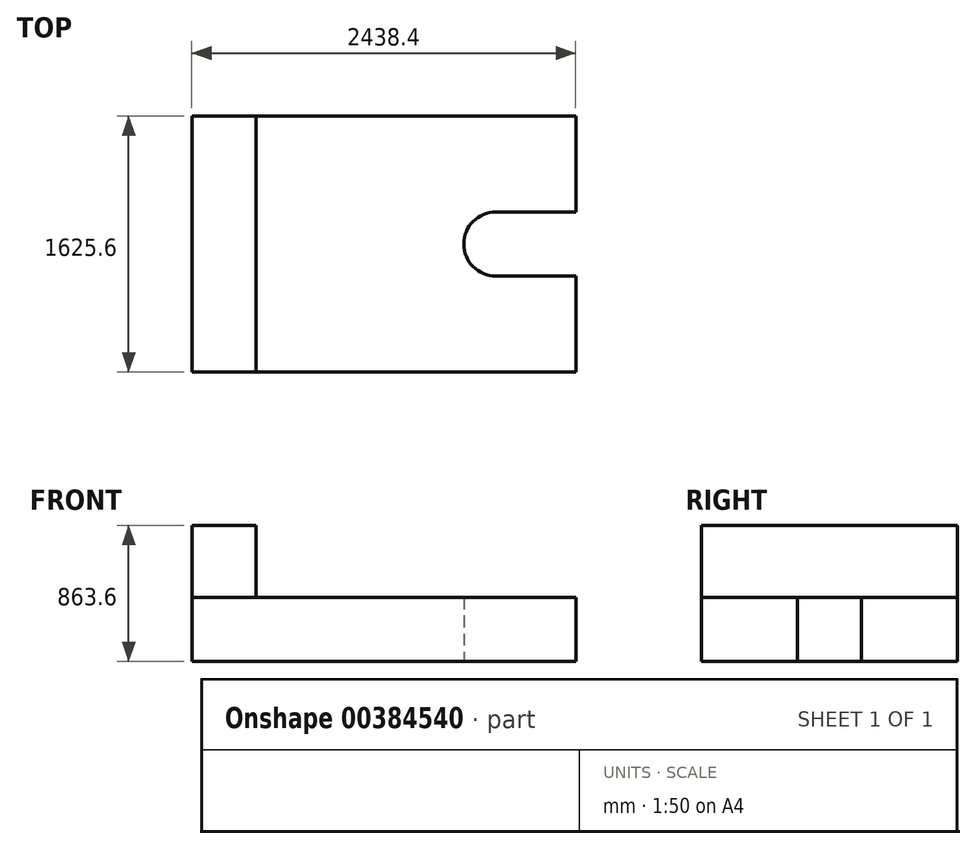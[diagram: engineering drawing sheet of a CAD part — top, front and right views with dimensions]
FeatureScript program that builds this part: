
annotation { "Feature Type Name" : "Feature", "Feature Type Description" : "" }
export const myFeature = defineFeature(function(context is Context, id is Id, definition is map)
    precondition{}
    {
        {
            var Q0;
            Q0=qCreatedBy(makeId("Top.planeOp"),FACE);
            var sketch = newSketch(context, id + "F0", { "sketchPlane" : qUnion([Q0])});
            skLineSegment(sketch, "E0", {"start": v(-60.74, 0) * mm, "end": v(-60.74, 1625.6) * mm});
            skLineSegment(sketch, "E1", {"start": v(-60.74, 1625.6) * mm, "end": v(2377.66, 1625.6) * mm});
            skLineSegment(sketch, "E2", {"start": v(2377.66, 1625.6) * mm, "end": v(2377.66, 0) * mm});
            skLineSegment(sketch, "E3", {"start": v(2377.66, 0) * mm, "end": v(-60.74, 0) * mm});
            skSolve(sketch);
        }
        {
            var Q0;
            Q0=makeQuery(id+"F0.imprint","IMPRINT",FACE,{"disambiguationData":[TD([[makeQuery(id+"F0.imprint","IMPRINT",EDGE,{"derivedFrom":sQuery(id+"F0.wireOp",EDGE,"E0")}),-1.0]])]});
            extrude(context, id + "F1", {"entities" : qUnion([Q0]), "depth" : 406.4 * mm});
        }
        {
            var Q0;
            Q0=makeQuery(id+"F1.opExtrude","CAP_FACE",FACE,{"disambiguationData":[OSD([sQuery(id+"F0.wireOp",EDGE,"E0"),sQuery(id+"F0.wireOp",EDGE,"E1"),sQuery(id+"F0.wireOp",EDGE,"E2"),sQuery(id+"F0.wireOp",EDGE,"E3")])],"isStart":true});
            var sketch = newSketch(context, id + "F2", { "sketchPlane" : qUnion([Q0])});
            skLineSegment(sketch, "E4", {"start": v(2377.66, -609.6) * mm, "end": v(1869.66, -609.6) * mm});
            skLineSegment(sketch, "E5", {"start": v(2377.66, -1016) * mm, "end": v(1869.66, -1016) * mm});
            skArc(sketch, "E6", {"start": v(1869.66, -609.6) * mm, "mid": v(1666.46, -812.8) * mm, "end": v(1869.66, -1016) * mm});
            skSolve(sketch);
        }
        {
            var Q0;
            {var subQ0=sQuery(id+"F2.wireOp",EDGE,"E4");Q0=makeQuery(id+"F2.imprint","IMPRINT",FACE,{"disambiguationData":[TD([[makeQuery(id+"F2.imprint","IMPRINT",EDGE,{"derivedFrom":subQ0}),1.0]])]});}
            extrude(context, id + "F3", {"entities" : qUnion([Q0]), "operationType" : NewBodyOperationType.REMOVE, "oppositeDirection" : true, "depth" : 406.4 * mm});
        }
        {
            var Q0;
            Q0=makeQuery(id+"F1.opExtrude","SWEPT_FACE",FACE,{"disambiguationData":[OSD([sQuery(id+"F0.wireOp",EDGE,"E1")])]});
            var sketch = newSketch(context, id + "F4", { "sketchPlane" : qUnion([Q0])});
            skLineSegment(sketch, "E7", {"start": v(60.74, 406.4) * mm, "end": v(60.74, 863.6) * mm});
            skLineSegment(sketch, "E8", {"start": v(60.74, 863.6) * mm, "end": v(-345.66, 863.6) * mm});
            skLineSegment(sketch, "E9", {"start": v(-345.66, 863.6) * mm, "end": v(-345.66, 406.4) * mm});
            skSolve(sketch);
        }
        {
            var Q0;
            {var subQ0=sQuery(id+"F4.wireOp",EDGE,"E7");Q0=makeQuery(id+"F4.imprint","IMPRINT",FACE,{"disambiguationData":[TD([[makeQuery(id+"F4.imprint","IMPRINT",EDGE,{"derivedFrom":subQ0}),1.0]])]});}
            extrude(context, id + "F5", {"entities" : qUnion([Q0]), "oppositeDirection" : true, "depth" : 1625.6 * mm});
        }
    });
